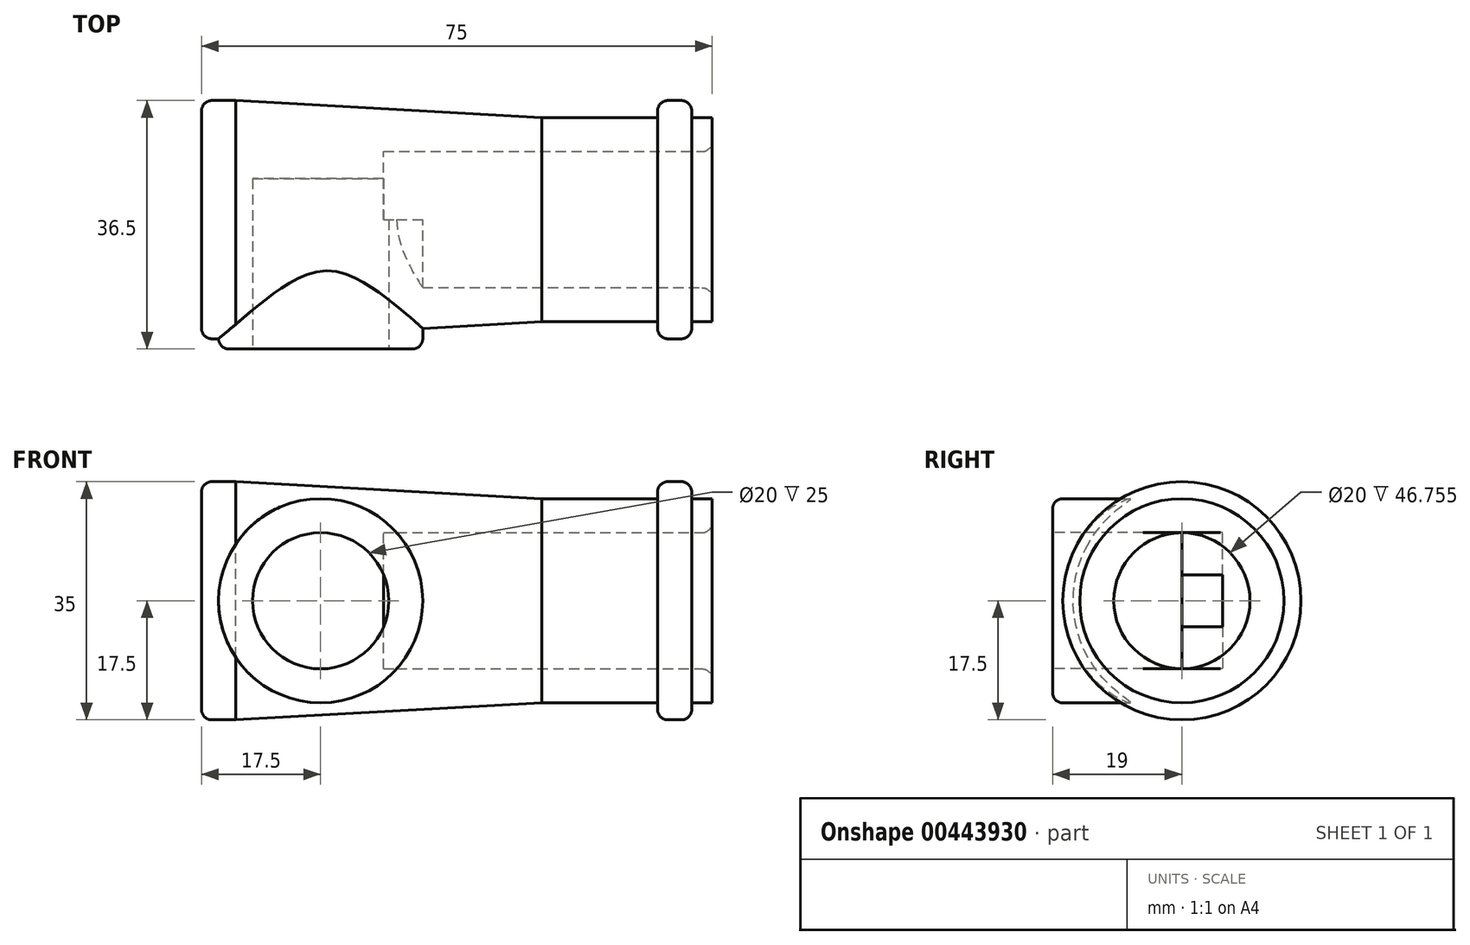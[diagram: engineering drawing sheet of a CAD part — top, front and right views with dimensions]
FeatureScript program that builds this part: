
annotation { "Feature Type Name" : "Feature", "Feature Type Description" : "" }
export const myFeature = defineFeature(function(context is Context, id is Id, definition is map)
    precondition{}
    {
        {
            var Q0;
            Q0=qCreatedBy(makeId("Front.planeOp"),FACE);
            var sketch = newSketch(context, id + "F0", { "sketchPlane" : qUnion([Q0])});
            skLineSegment(sketch, "E0", {"start": v(0, 0) * mm, "end": v(0, 17.5) * mm});
            skLineSegment(sketch, "E1", {"start": v(0, 17.5) * mm, "end": v(5, 17.5) * mm});
            skLineSegment(sketch, "E2", {"start": v(5, 17.5) * mm, "end": v(50, 15) * mm});
            skLineSegment(sketch, "E3", {"start": v(50, 15) * mm, "end": v(67, 15) * mm});
            skLineSegment(sketch, "E4", {"start": v(67, 15) * mm, "end": v(67, 17.5) * mm});
            skLineSegment(sketch, "E5", {"start": v(67, 17.5) * mm, "end": v(72, 17.5) * mm});
            skLineSegment(sketch, "E6", {"start": v(72, 17.5) * mm, "end": v(72, 15) * mm});
            skLineSegment(sketch, "E7", {"start": v(72, 15) * mm, "end": v(75, 15) * mm});
            skLineSegment(sketch, "E8", {"start": v(75, 15) * mm, "end": v(75, 10) * mm});
            skLineSegment(sketch, "E9", {"start": v(75, 10) * mm, "end": v(26.74, 10) * mm});
            skLineSegment(sketch, "E10", {"start": v(26.74, 10) * mm, "end": v(26.74, 0) * mm});
            skLineSegment(sketch, "E11", {"start": v(26.74, 0) * mm, "end": v(0, 0) * mm});
            skSolve(sketch);
        }
        {
            var Q0;
            Q0 = qSketchRegion(id + "F0", true);
            var Q1;
            Q1=sQuery(id+"F0.wireOp",EDGE,"E11");
            revolve(context, id + "F1", {"entities" : qUnion([Q0]), "axis" : qUnion([Q1]), "revolveType" : RevolveType.FULL});
        }
        {
            var Q0;
            Q0=qCreatedBy(makeId("Front.planeOp"),FACE);
            var sketch = newSketch(context, id + "F2", { "sketchPlane" : qUnion([Q0])});
            skCircle(sketch, "E12", {"center": v(17.5, 0) * mm, "radius": 15 * mm});
            skSolve(sketch);
        }
        {
            var Q0;
            Q0 = qSketchRegion(id + "F2", true);
            extrude(context, id + "F3", {"entities" : qUnion([Q0]), "operationType" : NewBodyOperationType.ADD, "depth" : 19 * mm});
        }
        {
            var Q0;
            Q0=makeQuery(id+"F3.opExtrude","CAP_FACE",FACE,{"disambiguationData":[OSD([sQuery(id+"F2.wireOp",EDGE,"E12")])],"isStart":false});
            var sketch = newSketch(context, id + "F4", { "sketchPlane" : qUnion([Q0])});
            skCircle(sketch, "E13", {"center": v(17.5, 0) * mm, "radius": 10 * mm});
            skSolve(sketch);
        }
        {
            var Q0;
            Q0 = qSketchRegion(id + "F4", true);
            extrude(context, id + "F5", {"entities" : qUnion([Q0]), "operationType" : NewBodyOperationType.REMOVE, "oppositeDirection" : true, "depth" : 25 * mm});
        }
        {
            var Q0;
            Q0=makeQuery(id+"F3.opExtrude","CAP_EDGE",EDGE,{"disambiguationData":[OSD([sQuery(id+"F2.wireOp",EDGE,"E12")])],"isStart":false});
            var Q1;
            Q1=makeQuery(id+"F1.opRevolve","SWEPT_EDGE",EDGE,{"disambiguationData":[OSD([sQuery(id+"F0.wireOp",EDGE,"E0"),sQuery(id+"F0.wireOp",EDGE,"E1")])]});
            var Q2;
            Q2=makeQuery(id+"F1.opRevolve","SWEPT_EDGE",EDGE,{"disambiguationData":[OSD([sQuery(id+"F0.wireOp",EDGE,"E4"),sQuery(id+"F0.wireOp",EDGE,"E5")])]});
            var Q3;
            Q3=makeQuery(id+"F1.opRevolve","SWEPT_EDGE",EDGE,{"disambiguationData":[OSD([sQuery(id+"F0.wireOp",EDGE,"E5"),sQuery(id+"F0.wireOp",EDGE,"E6")])]});
            var Q4;
            Q4=makeQuery(id+"F1.opRevolve","SWEPT_EDGE",EDGE,{"disambiguationData":[OSD([sQuery(id+"F0.wireOp",EDGE,"E8"),sQuery(id+"F0.wireOp",EDGE,"E9")])]});
            fillet(context, id + "F6", {"entities" : qUnion([Q0, Q1, Q2, Q3, Q4]), "radius" : 1.5 * mm, "tangentPropagation" : true, "allowEdgeOverflow" : false});
        }
    });
